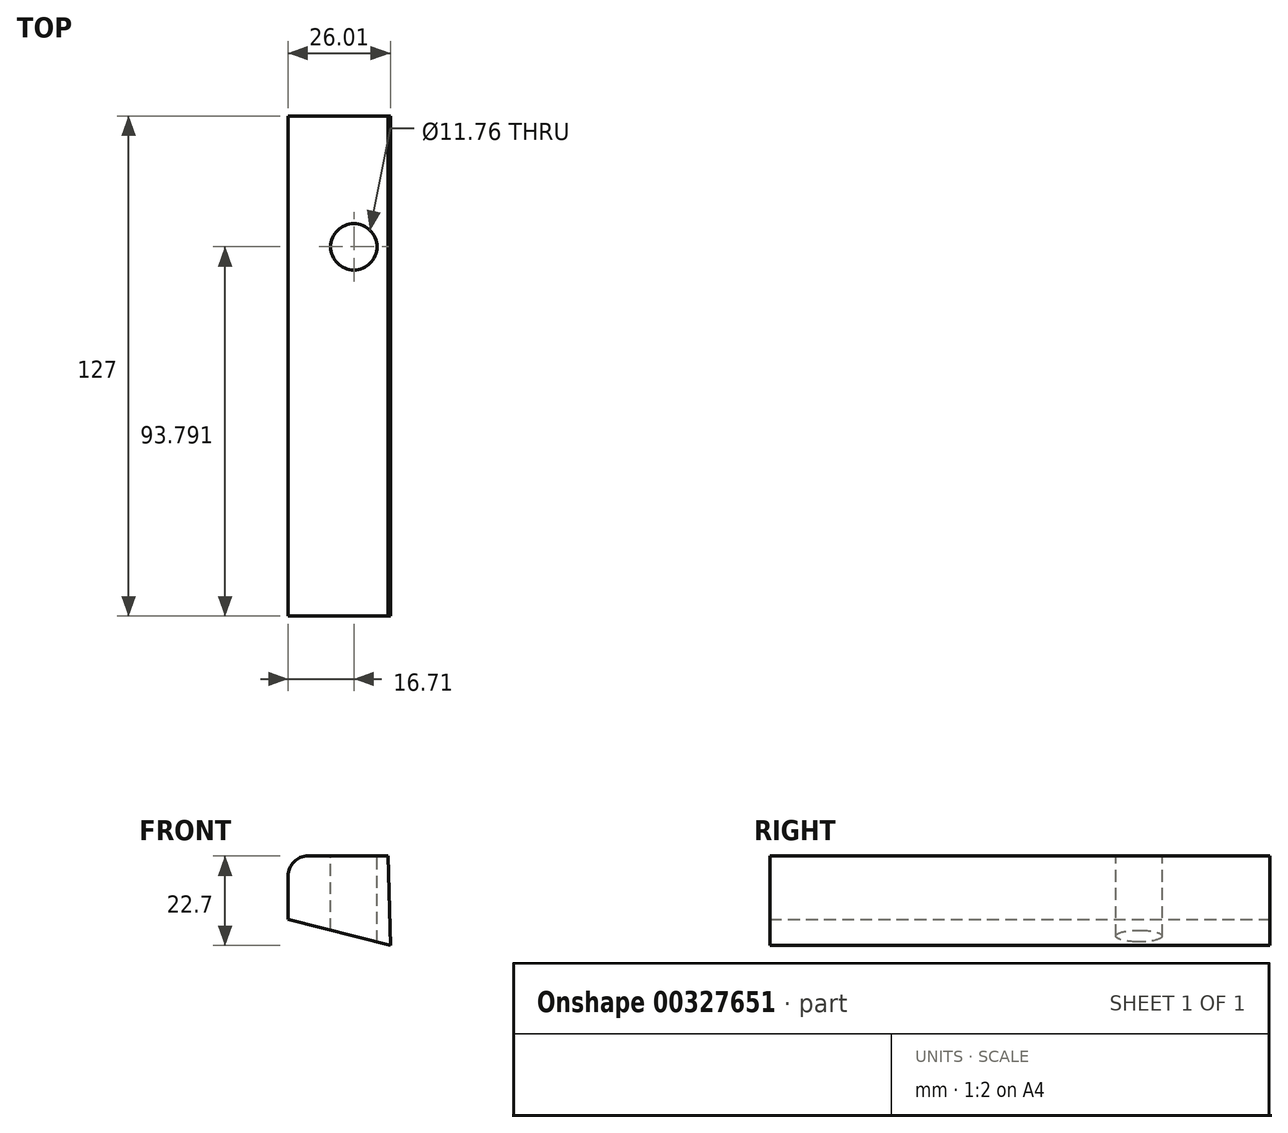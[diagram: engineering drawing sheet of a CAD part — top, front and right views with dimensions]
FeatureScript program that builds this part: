
annotation { "Feature Type Name" : "Feature", "Feature Type Description" : "" }
export const myFeature = defineFeature(function(context is Context, id is Id, definition is map)
    precondition{}
    {
        {
            var Q0;
            Q0=qCreatedBy(makeId("Front.planeOp"),FACE);
            var sketch = newSketch(context, id + "F0", { "sketchPlane" : qUnion([Q0])});
            skLineSegment(sketch, "E0", {"start": v(-16.7, -3.98) * mm, "end": v(-16.7, 12.1) * mm});
            skLineSegment(sketch, "E1", {"start": v(-16.7, 12.1) * mm, "end": v(8.7, 12.1) * mm});
            skLineSegment(sketch, "E2", {"start": v(8.7, 12.1) * mm, "end": v(9.3, -10.6) * mm});
            skLineSegment(sketch, "E3", {"start": v(9.3, -10.6) * mm, "end": v(-16.7, -3.98) * mm});
            skSolve(sketch);
        }
        {
            var Q0;
            Q0 = qSketchRegion(id + "F0", true);
            extrude(context, id + "F1", {"entities" : qUnion([Q0]), "endBound" : BoundingType.SYMMETRIC, "depth" : 127 * mm});
        }
        {
            var Q0;
            Q0=makeQuery(id+"F1.opExtrude","SWEPT_EDGE",EDGE,{"disambiguationData":[OSD([sQuery(id+"F0.wireOp",EDGE,"E0"),sQuery(id+"F0.wireOp",EDGE,"E1")])]});
            fillet(context, id + "F2", {"entities" : qUnion([Q0]), "radius" : 5.08 * mm, "tangentPropagation" : true, "allowEdgeOverflow" : false});
        }
        {
            var Q0;
            Q0=makeQuery(id+"F1.opExtrude","SWEPT_FACE",FACE,{"disambiguationData":[OSD([sQuery(id+"F0.wireOp",EDGE,"E1")])]});
            var sketch = newSketch(context, id + "F3", { "sketchPlane" : qUnion([Q0])});
            skCircle(sketch, "E4", {"center": v(0, 30.3) * mm, "radius": 5.88 * mm});
            skSolve(sketch);
        }
        {
            var Q0;
            Q0 = qSketchRegion(id + "F3", true);
            extrude(context, id + "F4", {"entities" : qUnion([Q0]), "operationType" : NewBodyOperationType.REMOVE, "oppositeDirection" : true, "depth" : 25.4 * mm});
        }
    });
